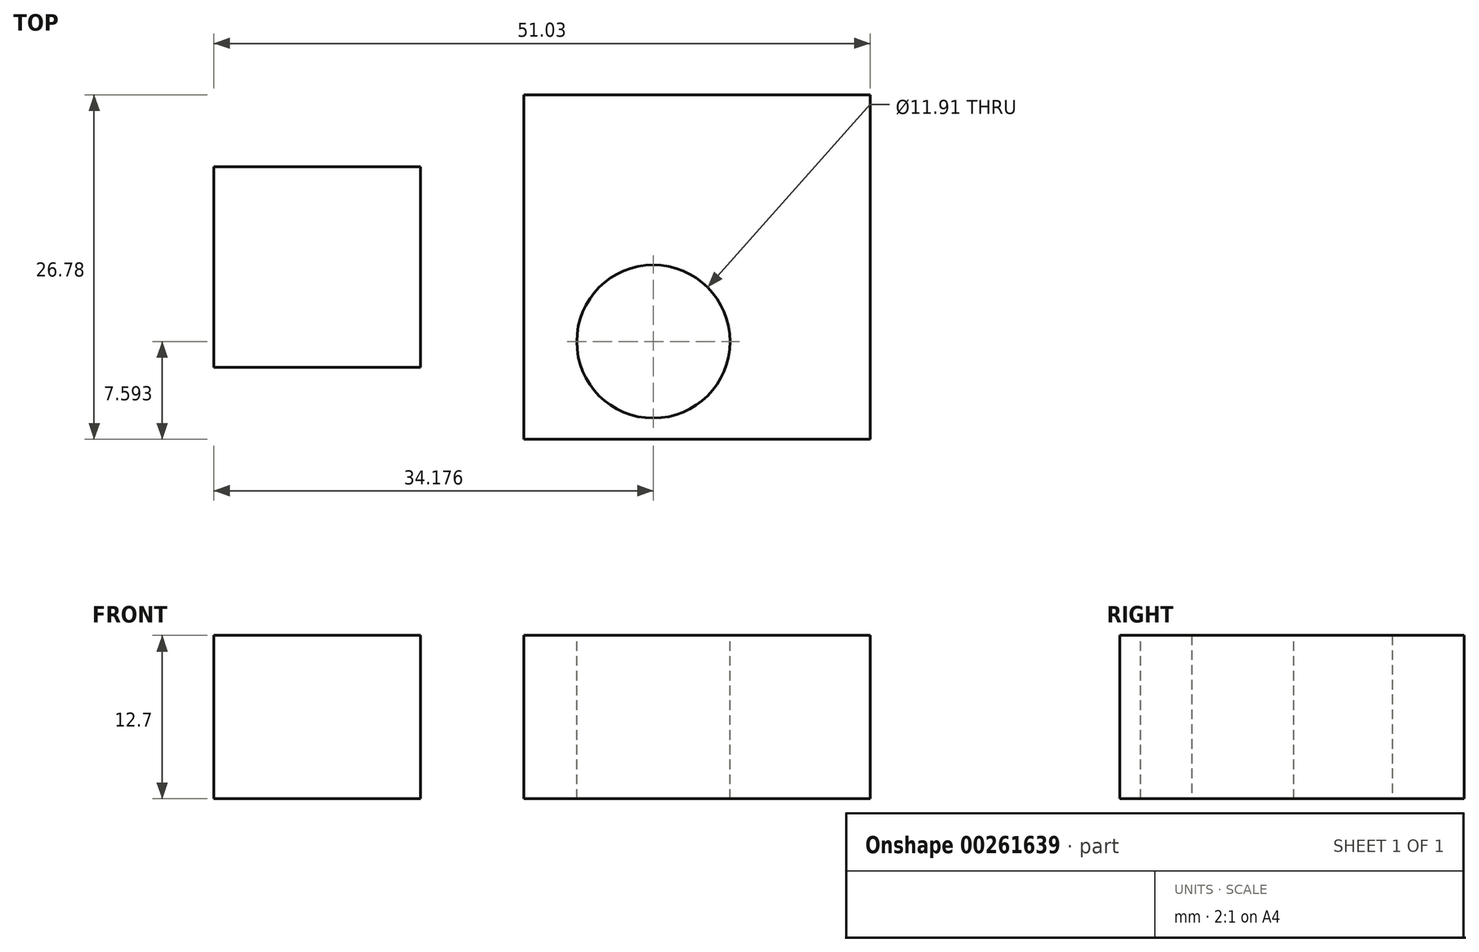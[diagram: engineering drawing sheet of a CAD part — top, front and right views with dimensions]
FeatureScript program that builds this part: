
annotation { "Feature Type Name" : "Feature", "Feature Type Description" : "" }
export const myFeature = defineFeature(function(context is Context, id is Id, definition is map)
    precondition{}
    {
        {
            var Q0;
            Q0=qCreatedBy(makeId("Top.planeOp"),FACE);
            var sketch = newSketch(context, id + "F0", { "sketchPlane" : qUnion([Q0])});
            skLineSegment(sketch, "E0.bottom", {"start": v(8.04, -7.79) * mm, "end": v(-8.04, -7.79) * mm});
            skLineSegment(sketch, "E0.top", {"start": v(8.04, 7.79) * mm, "end": v(-8.04, 7.79) * mm});
            skLineSegment(sketch, "E0.left", {"start": v(8.04, -7.79) * mm, "end": v(8.04, 7.79) * mm});
            skLineSegment(sketch, "E0.right", {"start": v(-8.04, -7.79) * mm, "end": v(-8.04, 7.79) * mm});
            skPoint(sketch, "E0.middle", {"position": v(0, 0) * mm});
            skSolve(sketch);
        }
        {
            var Q0;
            Q0 = qSketchRegion(id + "F0", true);
            extrude(context, id + "F1", {"entities" : qUnion([Q0]), "depth" : 12.7 * mm});
        }
        {
            var Q0;
            Q0=qCreatedBy(makeId("Top.planeOp"),FACE);
            var sketch = newSketch(context, id + "F2", { "sketchPlane" : qUnion([Q0])});
            skLineSegment(sketch, "E1.bottom", {"start": v(42.99, -13.4) * mm, "end": v(16.08, -13.4) * mm});
            skLineSegment(sketch, "E1.top", {"start": v(42.99, 13.4) * mm, "end": v(16.08, 13.4) * mm});
            skLineSegment(sketch, "E1.left", {"start": v(42.99, -13.4) * mm, "end": v(42.99, 13.4) * mm});
            skLineSegment(sketch, "E1.right", {"start": v(16.08, -13.4) * mm, "end": v(16.08, 13.4) * mm});
            skPoint(sketch, "E1.middle", {"position": v(29.53, 0) * mm});
            skPoint(sketch, "E2", {"position": v(22.32, -4.8) * mm});
            skSolve(sketch);
        }
        {
            var Q0;
            Q0=makeQuery(id+"F2.imprint","IMPRINT",FACE,{"disambiguationData":[TD([[makeQuery(id+"F2.imprint","IMPRINT",EDGE,{"derivedFrom":sQuery(id+"F2.wireOp",EDGE,"E1.bottom")}),-1.0]])]});
            extrude(context, id + "F3", {"entities" : qUnion([Q0]), "depth" : 12.7 * mm});
        }
        {
            var Q0;
            Q0=makeQuery(id+"F3.opExtrude","CAP_FACE",FACE,{"disambiguationData":[OSD([sQuery(id+"F2.wireOp",EDGE,"E1.bottom"),sQuery(id+"F2.wireOp",EDGE,"E1.top"),sQuery(id+"F2.wireOp",EDGE,"E1.left"),sQuery(id+"F2.wireOp",EDGE,"E1.right")])],"isStart":false});
            var sketch = newSketch(context, id + "F4", { "sketchPlane" : qUnion([Q0])});
            skPoint(sketch, "E3", {"position": v(26.14, -5.8) * mm});
            skSolve(sketch);
        }
        {
            var Q0;
            Q0=sQuery(id+"F4.wireOp",VERTEX,"E3");
            var Q1;
            Q1=makeQuery(id+"F3.opExtrude","SWEPT_BODY",BODY,{"disambiguationData":[OSD([sQuery(id+"F2.wireOp",EDGE,"E1.bottom"),sQuery(id+"F2.wireOp",EDGE,"E1.top"),sQuery(id+"F2.wireOp",EDGE,"E1.left"),sQuery(id+"F2.wireOp",EDGE,"E1.right")])]});
            hole(context, id + "F5", {"style" : HoleStyle.SIMPLE, "endStyle" : HoleEndStyle.THROUGH, "standardTappedOrClearance" : lookupTablePath({ "standard" : "ANSI", "engagement" : "75%", "pitch" : "28 tpi", "size" : "1/2", "type" : "Tapped" }), "standardBlindInLast" : lookupTablePath({ "standard" : "ANSI", "engagement" : "75%", "pitch" : "28 tpi", "size" : "1/2", "type" : "Tapped" }), "holeDiameter" : 11.9 * mm, "showTappedDepth" : true, "tappedDepth" : 12.7 * mm, "tapClearance" : 3, "locations" : qUnion([Q0]), "scope" : qUnion([Q1]), "majorDiameter" : 12.7 * mm});
        }
    });
